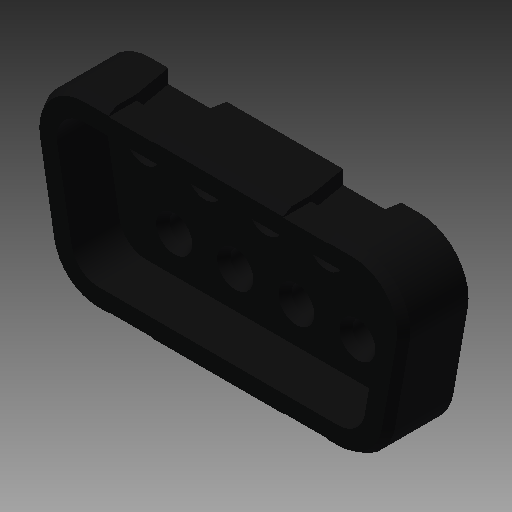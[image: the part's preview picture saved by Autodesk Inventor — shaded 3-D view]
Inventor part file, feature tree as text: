
AUTODESK INVENTOR PART (.ipt)
format: ipt  version: 2017 (Build 210142000, 142)  size: 209,920 bytes
history: native  units: in
note: dims shown in document units (in); Inventor stores cm internally (conversion verified against a paired STEP export)
features: chamfer x1
ambient origin geometry x8: Origin, YZ Plane, XZ Plane, XY Plane, X Axis, Y Axis, Z Axis, Center Point
bodies: Solid1 (feature_tree)
feature tree (1):
  chamfer  "Chamfer2"  [1 undecoded]
note: 1 required parameter value undecoded (feature->parameter linkage not recoverable at this tier; creation-order binding heuristic only, values carry confidence <= 0.55)
